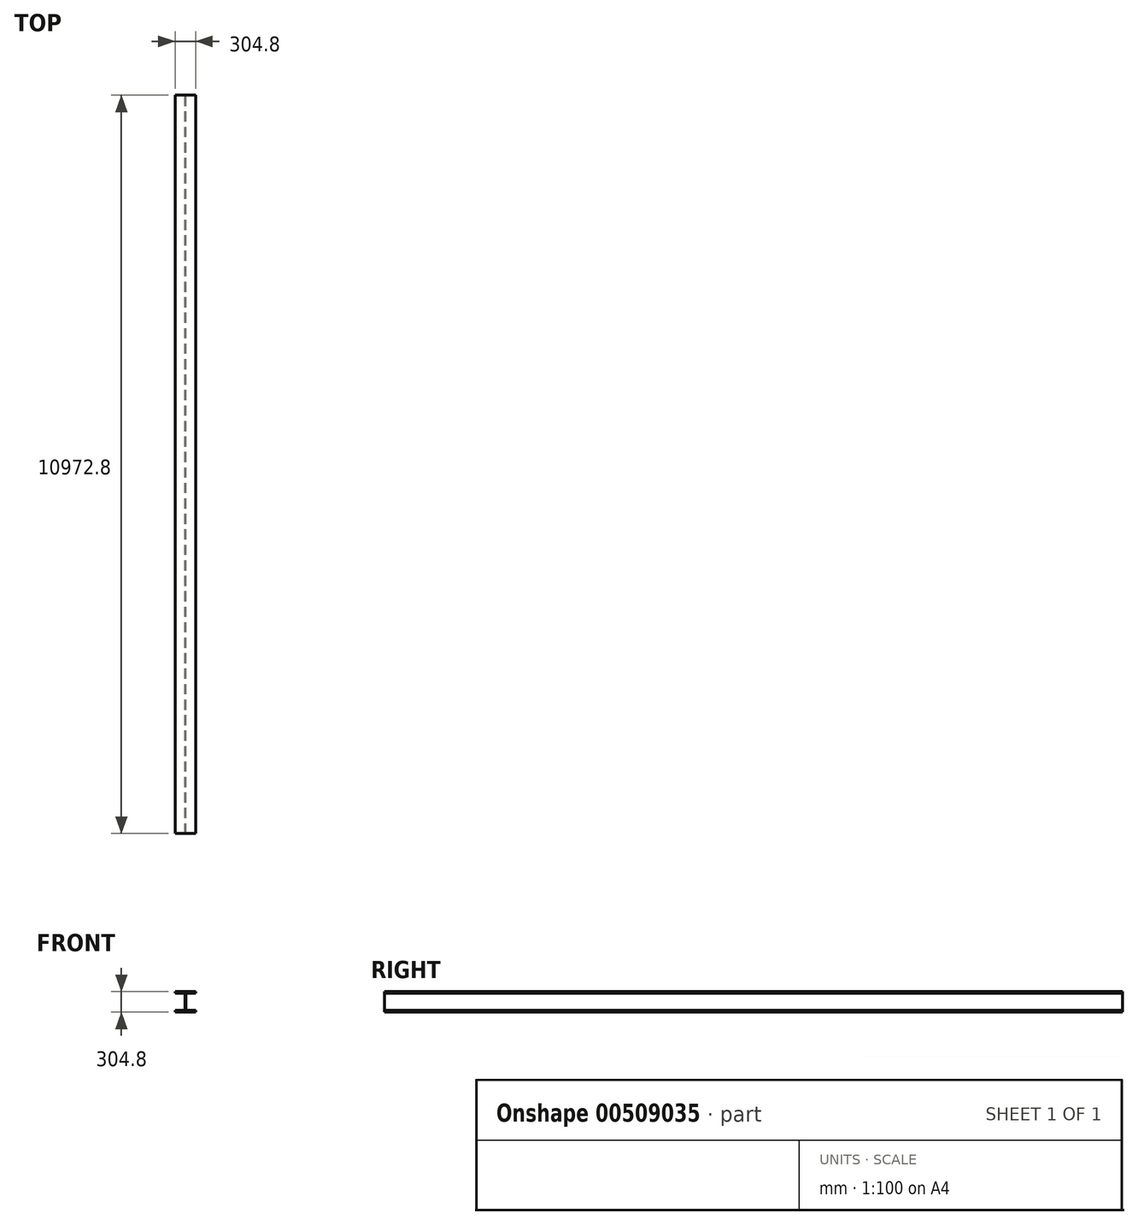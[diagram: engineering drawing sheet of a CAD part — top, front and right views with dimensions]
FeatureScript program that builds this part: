
annotation { "Feature Type Name" : "Feature", "Feature Type Description" : "" }
export const myFeature = defineFeature(function(context is Context, id is Id, definition is map)
    precondition{}
    {
        {
            var Q0;
            Q0=qCreatedBy(makeId("Front.planeOp"),FACE);
            var sketch = newSketch(context, id + "F0", { "sketchPlane" : qUnion([Q0])});
            skLineSegment(sketch, "E0", {"start": v(152.4, -127) * mm, "end": v(8.89, -127) * mm});
            skLineSegment(sketch, "E1", {"start": v(6.35, -124.46) * mm, "end": v(6.35, 124.46) * mm});
            skLineSegment(sketch, "E2", {"start": v(8.89, 127) * mm, "end": v(152.4, 127) * mm});
            skLineSegment(sketch, "E3", {"start": v(-152.4, 127) * mm, "end": v(-8.89, 127) * mm});
            skLineSegment(sketch, "E4", {"start": v(-6.35, 124.46) * mm, "end": v(-6.35, -124.46) * mm});
            skLineSegment(sketch, "E5", {"start": v(-8.89, -127) * mm, "end": v(-152.4, -127) * mm});
            skLineSegment(sketch, "E6", {"start": v(0, 0) * mm, "end": v(-6.35, 0) * mm, "construction": true});
            skLineSegment(sketch, "E7", {"start": v(0, 0) * mm, "end": v(6.35, 0) * mm, "construction": true});
            skLineSegment(sketch, "E8", {"start": v(0, 0) * mm, "end": v(0, 152.4) * mm, "construction": true});
            skLineSegment(sketch, "E9", {"start": v(0, 0) * mm, "end": v(0, -152.4) * mm, "construction": true});
            skPoint(sketch, "E10.visualSharp", {"position": v(-6.35, 127) * mm});
            skArc(sketch, "E10.filletArc", {"start": v(-6.35, 124.46) * mm, "mid": v(-7.1, 126.26) * mm, "end": v(-8.89, 127) * mm});
            skPoint(sketch, "E11.visualSharp", {"position": v(6.35, 127) * mm});
            skArc(sketch, "E11.filletArc", {"start": v(8.89, 127) * mm, "mid": v(7.1, 126.26) * mm, "end": v(6.35, 124.46) * mm});
            skPoint(sketch, "E12.visualSharp", {"position": v(6.35, -127) * mm});
            skArc(sketch, "E12.filletArc", {"start": v(6.35, -124.46) * mm, "mid": v(7.1, -126.26) * mm, "end": v(8.89, -127) * mm});
            skPoint(sketch, "E13.visualSharp", {"position": v(-6.35, -127) * mm});
            skArc(sketch, "E13.filletArc", {"start": v(-8.9, -127) * mm, "mid": v(-7.1, -126.26) * mm, "end": v(-6.35, -124.46) * mm});
            skPoint(sketch, "E14.visualSharp", {"position": v(-152.4, 152.4) * mm});
            skPoint(sketch, "E15.visualSharp", {"position": v(152.4, 152.4) * mm});
            skPoint(sketch, "E16.visualSharp", {"position": v(152.4, 127) * mm});
            skPoint(sketch, "E17.visualSharp", {"position": v(152.4, -152.4) * mm});
            skPoint(sketch, "E18.visualSharp", {"position": v(-152.4, -127) * mm});
            skPoint(sketch, "E19.visualSharp", {"position": v(-152.4, -152.4) * mm});
            skLineSegment(sketch, "E20", {"start": v(152.4, -127) * mm, "end": v(152.4, -152.4) * mm});
            skLineSegment(sketch, "E21", {"start": v(-152.4, -127) * mm, "end": v(-152.4, -152.4) * mm});
            skLineSegment(sketch, "E22", {"start": v(-152.4, 152.4) * mm, "end": v(-152.4, 127) * mm});
            skLineSegment(sketch, "E23", {"start": v(152.4, 152.4) * mm, "end": v(152.4, 127) * mm});
            skLineSegment(sketch, "E24", {"start": v(-152.4, 152.4) * mm, "end": v(152.4, 152.4) * mm});
            skLineSegment(sketch, "E25", {"start": v(-152.4, -152.4) * mm, "end": v(152.4, -152.4) * mm});
            skSolve(sketch);
        }
        {
            var Q0;
            Q0=makeQuery(id+"F0.imprint","IMPRINT",FACE,{"disambiguationData":[TD([[makeQuery(id+"F0.imprint","IMPRINT",EDGE,{"derivedFrom":sQuery(id+"F0.wireOp",EDGE,"E0")}),1.0]])]});
            extrude(context, id + "F1", {"entities" : qUnion([Q0]), "depth" : 10972.8 * mm});
        }
    });
